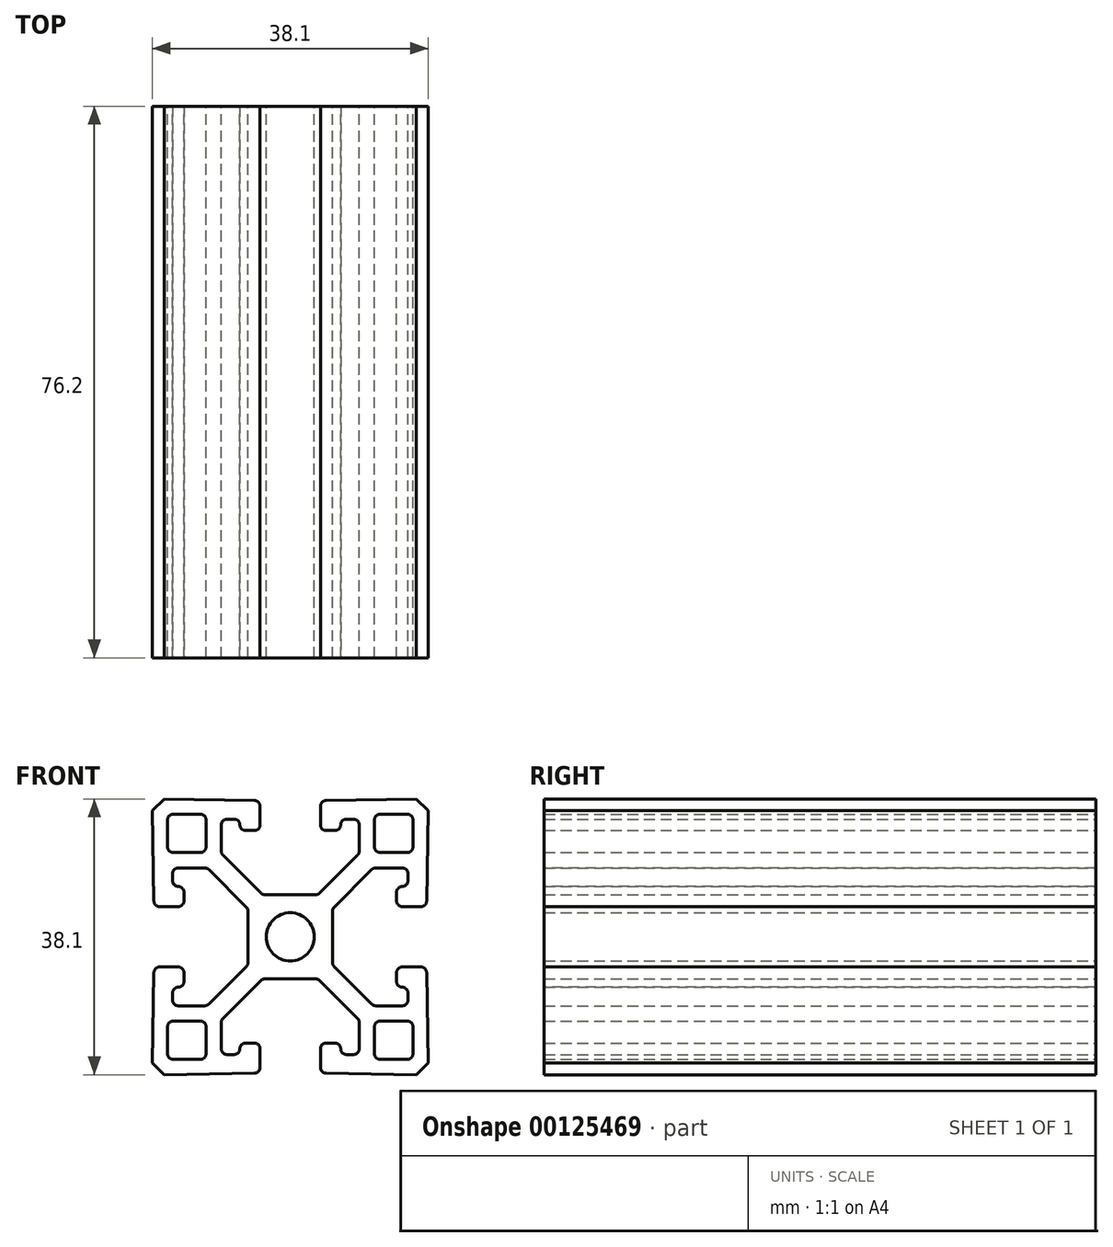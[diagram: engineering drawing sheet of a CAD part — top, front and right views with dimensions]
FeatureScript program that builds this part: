
annotation { "Feature Type Name" : "Feature", "Feature Type Description" : "" }
export const myFeature = defineFeature(function(context is Context, id is Id, definition is map)
    precondition{}
    {
        {
            var Q0;
            Q0=qCreatedBy(makeId("Front.planeOp"),FACE);
            var sketch = newSketch(context, id + "F0", { "sketchPlane" : qUnion([Q0])});
            skCircle(sketch, "E0", {"center": v(-50.07, 14.42) * mm, "radius": 3.33 * mm});
            skLineSegment(sketch, "E1", {"start": v(-33.92, -2.52) * mm, "end": v(-37.65, -2.52) * mm});
            skArc(sketch, "E2", {"start": v(-37.65, -2.52) * mm, "mid": v(-38.2, -2.3) * mm, "end": v(-38.44, -1.74) * mm});
            skLineSegment(sketch, "E3", {"start": v(-38.44, -1.74) * mm, "end": v(-38.44, 2) * mm});
            skArc(sketch, "E4", {"start": v(-38.44, 2) * mm, "mid": v(-38.2, 2.56) * mm, "end": v(-37.65, 2.79) * mm});
            skLineSegment(sketch, "E5", {"start": v(-37.65, 2.79) * mm, "end": v(-33.92, 2.79) * mm});
            skArc(sketch, "E6", {"start": v(-33.92, 2.79) * mm, "mid": v(-33.36, 2.56) * mm, "end": v(-33.13, 2) * mm});
            skLineSegment(sketch, "E7", {"start": v(-33.13, 2) * mm, "end": v(-33.13, -1.74) * mm});
            skArc(sketch, "E8", {"start": v(-33.13, -1.74) * mm, "mid": v(-33.36, -2.3) * mm, "end": v(-33.92, -2.52) * mm});
            skLineSegment(sketch, "E9", {"start": v(-67.01, 2) * mm, "end": v(-67.01, -1.74) * mm});
            skArc(sketch, "E10", {"start": v(-67.01, -1.74) * mm, "mid": v(-66.78, -2.3) * mm, "end": v(-66.23, -2.52) * mm});
            skLineSegment(sketch, "E11", {"start": v(-66.23, -2.52) * mm, "end": v(-62.5, -2.52) * mm});
            skArc(sketch, "E12", {"start": v(-62.5, -2.52) * mm, "mid": v(-61.93, -2.3) * mm, "end": v(-61.7, -1.74) * mm});
            skLineSegment(sketch, "E13", {"start": v(-61.7, -1.74) * mm, "end": v(-61.7, 2) * mm});
            skArc(sketch, "E14", {"start": v(-61.7, 2) * mm, "mid": v(-61.93, 2.56) * mm, "end": v(-62.5, 2.79) * mm});
            skLineSegment(sketch, "E15", {"start": v(-62.5, 2.79) * mm, "end": v(-66.23, 2.79) * mm});
            skArc(sketch, "E16", {"start": v(-66.23, 2.79) * mm, "mid": v(-66.78, 2.56) * mm, "end": v(-67.01, 2) * mm});
            skLineSegment(sketch, "E17", {"start": v(-67.01, 30.57) * mm, "end": v(-67.01, 26.84) * mm});
            skArc(sketch, "E18", {"start": v(-67.01, 26.84) * mm, "mid": v(-66.78, 26.28) * mm, "end": v(-66.23, 26.05) * mm});
            skLineSegment(sketch, "E19", {"start": v(-66.23, 26.05) * mm, "end": v(-62.5, 26.05) * mm});
            skArc(sketch, "E20", {"start": v(-62.5, 26.05) * mm, "mid": v(-61.93, 26.28) * mm, "end": v(-61.7, 26.84) * mm});
            skLineSegment(sketch, "E21", {"start": v(-61.7, 26.84) * mm, "end": v(-61.7, 30.57) * mm});
            skArc(sketch, "E22", {"start": v(-61.7, 30.57) * mm, "mid": v(-61.93, 31.13) * mm, "end": v(-62.5, 31.36) * mm});
            skLineSegment(sketch, "E23", {"start": v(-62.5, 31.36) * mm, "end": v(-66.23, 31.36) * mm});
            skArc(sketch, "E24", {"start": v(-66.23, 31.36) * mm, "mid": v(-66.78, 31.13) * mm, "end": v(-67.01, 30.57) * mm});
            skArc(sketch, "E25", {"start": v(-37.65, 26.05) * mm, "mid": v(-38.2, 26.28) * mm, "end": v(-38.44, 26.84) * mm});
            skLineSegment(sketch, "E26", {"start": v(-38.44, 26.84) * mm, "end": v(-38.44, 30.57) * mm});
            skArc(sketch, "E27", {"start": v(-38.44, 30.57) * mm, "mid": v(-38.2, 31.13) * mm, "end": v(-37.65, 31.36) * mm});
            skLineSegment(sketch, "E28", {"start": v(-37.65, 31.36) * mm, "end": v(-33.92, 31.36) * mm});
            skArc(sketch, "E29", {"start": v(-33.92, 31.36) * mm, "mid": v(-33.36, 31.13) * mm, "end": v(-33.13, 30.57) * mm});
            skLineSegment(sketch, "E30", {"start": v(-33.13, 30.57) * mm, "end": v(-33.13, 26.84) * mm});
            skArc(sketch, "E31", {"start": v(-33.13, 26.84) * mm, "mid": v(-33.36, 26.28) * mm, "end": v(-33.92, 26.05) * mm});
            skLineSegment(sketch, "E32", {"start": v(-33.92, 26.05) * mm, "end": v(-37.65, 26.05) * mm});
            skArc(sketch, "E33", {"start": v(-56.24, -0.26) * mm, "mid": v(-56.8, -0.5) * mm, "end": v(-57.03, -1.05) * mm});
            skLineSegment(sketch, "E34", {"start": v(-56.24, -0.26) * mm, "end": v(-55.02, -0.26) * mm});
            skArc(sketch, "E35", {"start": v(-54.24, -1.05) * mm, "mid": v(-54.47, -0.5) * mm, "end": v(-55.02, -0.26) * mm});
            skLineSegment(sketch, "E36", {"start": v(-54.24, -1.05) * mm, "end": v(-54.24, -3.63) * mm});
            skArc(sketch, "E37", {"start": v(-55.01, -4.41) * mm, "mid": v(-54.46, -4.18) * mm, "end": v(-54.24, -3.63) * mm});
            skLineSegment(sketch, "E38", {"start": v(-55.01, -4.41) * mm, "end": v(-67.5, -4.63) * mm});
            skLineSegment(sketch, "E39", {"start": v(-67.5, -4.63) * mm, "end": v(-69.12, -3) * mm});
            skLineSegment(sketch, "E40", {"start": v(-69.12, -3) * mm, "end": v(-68.9, 9.48) * mm});
            skArc(sketch, "E41", {"start": v(-68.12, 10.25) * mm, "mid": v(-68.67, 10.03) * mm, "end": v(-68.9, 9.48) * mm});
            skLineSegment(sketch, "E42", {"start": v(-68.12, 10.25) * mm, "end": v(-65.54, 10.25) * mm});
            skArc(sketch, "E43", {"start": v(-64.75, 9.47) * mm, "mid": v(-64.98, 10.02) * mm, "end": v(-65.54, 10.25) * mm});
            skLineSegment(sketch, "E44", {"start": v(-64.75, 9.47) * mm, "end": v(-64.75, 8.25) * mm});
            skArc(sketch, "E45", {"start": v(-65.54, 7.46) * mm, "mid": v(-64.98, 7.7) * mm, "end": v(-64.75, 8.25) * mm});
            skArc(sketch, "E46", {"start": v(-65.54, 7.46) * mm, "mid": v(-66.1, 7.23) * mm, "end": v(-66.33, 6.67) * mm});
            skLineSegment(sketch, "E47", {"start": v(-66.33, 6.67) * mm, "end": v(-66.33, 5.68) * mm});
            skArc(sketch, "E48", {"start": v(-66.33, 5.68) * mm, "mid": v(-66.1, 5.12) * mm, "end": v(-65.54, 4.9) * mm});
            skLineSegment(sketch, "E49", {"start": v(-65.54, 4.9) * mm, "end": v(-61.9, 4.9) * mm});
            skArc(sketch, "E50", {"start": v(-61.9, 4.9) * mm, "mid": v(-61.6, 4.95) * mm, "end": v(-61.34, 5.12) * mm});
            skLineSegment(sketch, "E51", {"start": v(-61.34, 5.12) * mm, "end": v(-56.12, 10.35) * mm});
            skArc(sketch, "E52", {"start": v(-56.12, 10.35) * mm, "mid": v(-55.95, 10.6) * mm, "end": v(-55.89, 10.9) * mm});
            skLineSegment(sketch, "E53", {"start": v(-55.89, 10.9) * mm, "end": v(-55.89, 17.93) * mm});
            skArc(sketch, "E54", {"start": v(-55.89, 17.93) * mm, "mid": v(-55.95, 18.24) * mm, "end": v(-56.12, 18.5) * mm});
            skLineSegment(sketch, "E55", {"start": v(-56.12, 18.5) * mm, "end": v(-61.34, 23.71) * mm});
            skArc(sketch, "E56", {"start": v(-61.34, 23.71) * mm, "mid": v(-61.6, 23.88) * mm, "end": v(-61.9, 23.94) * mm});
            skLineSegment(sketch, "E57", {"start": v(-61.9, 23.94) * mm, "end": v(-65.54, 23.94) * mm});
            skArc(sketch, "E58", {"start": v(-65.54, 23.94) * mm, "mid": v(-66.1, 23.71) * mm, "end": v(-66.33, 23.16) * mm});
            skLineSegment(sketch, "E59", {"start": v(-66.33, 23.16) * mm, "end": v(-66.33, 22.17) * mm});
            skArc(sketch, "E60", {"start": v(-66.33, 22.17) * mm, "mid": v(-66.1, 21.6) * mm, "end": v(-65.54, 21.38) * mm});
            skArc(sketch, "E61", {"start": v(-64.75, 20.6) * mm, "mid": v(-64.98, 21.15) * mm, "end": v(-65.54, 21.38) * mm});
            skLineSegment(sketch, "E62", {"start": v(-64.75, 20.6) * mm, "end": v(-64.75, 19.37) * mm});
            skArc(sketch, "E63", {"start": v(-65.54, 18.58) * mm, "mid": v(-64.98, 18.82) * mm, "end": v(-64.75, 19.37) * mm});
            skLineSegment(sketch, "E64", {"start": v(-65.54, 18.58) * mm, "end": v(-68.12, 18.58) * mm});
            skArc(sketch, "E65", {"start": v(-68.9, 19.36) * mm, "mid": v(-68.67, 18.81) * mm, "end": v(-68.12, 18.58) * mm});
            skLineSegment(sketch, "E66", {"start": v(-68.9, 19.36) * mm, "end": v(-69.12, 31.84) * mm});
            skLineSegment(sketch, "E67", {"start": v(-69.12, 31.84) * mm, "end": v(-67.5, 33.47) * mm});
            skLineSegment(sketch, "E68", {"start": v(-67.5, 33.47) * mm, "end": v(-55.01, 33.25) * mm});
            skArc(sketch, "E69", {"start": v(-54.24, 32.46) * mm, "mid": v(-54.46, 33.02) * mm, "end": v(-55.01, 33.25) * mm});
            skLineSegment(sketch, "E70", {"start": v(-54.24, 32.46) * mm, "end": v(-54.24, 29.89) * mm});
            skArc(sketch, "E71", {"start": v(-55.02, 29.1) * mm, "mid": v(-54.47, 29.33) * mm, "end": v(-54.24, 29.89) * mm});
            skLineSegment(sketch, "E72", {"start": v(-55.02, 29.1) * mm, "end": v(-56.24, 29.1) * mm});
            skArc(sketch, "E73", {"start": v(-57.03, 29.89) * mm, "mid": v(-56.8, 29.33) * mm, "end": v(-56.24, 29.1) * mm});
            skArc(sketch, "E74", {"start": v(-57.03, 29.89) * mm, "mid": v(-57.26, 30.44) * mm, "end": v(-57.82, 30.68) * mm});
            skLineSegment(sketch, "E75", {"start": v(-57.82, 30.68) * mm, "end": v(-58.8, 30.68) * mm});
            skArc(sketch, "E76", {"start": v(-58.8, 30.68) * mm, "mid": v(-59.37, 30.44) * mm, "end": v(-59.6, 29.89) * mm});
            skLineSegment(sketch, "E77", {"start": v(-59.6, 29.89) * mm, "end": v(-59.6, 26.25) * mm});
            skArc(sketch, "E78", {"start": v(-59.6, 26.25) * mm, "mid": v(-59.54, 25.94) * mm, "end": v(-59.37, 25.69) * mm});
            skLineSegment(sketch, "E79", {"start": v(-59.37, 25.69) * mm, "end": v(-54.14, 20.47) * mm});
            skArc(sketch, "E80", {"start": v(-54.14, 20.47) * mm, "mid": v(-53.89, 20.3) * mm, "end": v(-53.59, 20.24) * mm});
            skLineSegment(sketch, "E81", {"start": v(-53.59, 20.24) * mm, "end": v(-46.56, 20.24) * mm});
            skArc(sketch, "E82", {"start": v(-46.56, 20.24) * mm, "mid": v(-46.25, 20.3) * mm, "end": v(-46, 20.47) * mm});
            skLineSegment(sketch, "E83", {"start": v(-46, 20.47) * mm, "end": v(-40.78, 25.69) * mm});
            skArc(sketch, "E84", {"start": v(-40.78, 25.69) * mm, "mid": v(-40.6, 25.94) * mm, "end": v(-40.55, 26.25) * mm});
            skLineSegment(sketch, "E85", {"start": v(-40.55, 26.25) * mm, "end": v(-40.55, 29.89) * mm});
            skArc(sketch, "E86", {"start": v(-40.55, 29.89) * mm, "mid": v(-40.78, 30.44) * mm, "end": v(-41.33, 30.68) * mm});
            skLineSegment(sketch, "E87", {"start": v(-41.33, 30.68) * mm, "end": v(-42.32, 30.68) * mm});
            skArc(sketch, "E88", {"start": v(-42.32, 30.68) * mm, "mid": v(-42.88, 30.44) * mm, "end": v(-43.11, 29.89) * mm});
            skArc(sketch, "E89", {"start": v(-43.9, 29.1) * mm, "mid": v(-43.34, 29.33) * mm, "end": v(-43.11, 29.89) * mm});
            skLineSegment(sketch, "E90", {"start": v(-43.9, 29.1) * mm, "end": v(-45.12, 29.1) * mm});
            skArc(sketch, "E91", {"start": v(-45.9, 29.89) * mm, "mid": v(-45.67, 29.33) * mm, "end": v(-45.12, 29.1) * mm});
            skLineSegment(sketch, "E92", {"start": v(-45.9, 29.89) * mm, "end": v(-45.9, 32.46) * mm});
            skArc(sketch, "E93", {"start": v(-45.13, 33.25) * mm, "mid": v(-45.68, 33.02) * mm, "end": v(-45.9, 32.46) * mm});
            skLineSegment(sketch, "E94", {"start": v(-45.13, 33.25) * mm, "end": v(-32.65, 33.47) * mm});
            skLineSegment(sketch, "E95", {"start": v(-32.65, 33.47) * mm, "end": v(-31.02, 31.84) * mm});
            skLineSegment(sketch, "E96", {"start": v(-31.02, 31.84) * mm, "end": v(-31.24, 19.36) * mm});
            skArc(sketch, "E97", {"start": v(-32.03, 18.58) * mm, "mid": v(-31.47, 18.81) * mm, "end": v(-31.24, 19.36) * mm});
            skLineSegment(sketch, "E98", {"start": v(-32.03, 18.58) * mm, "end": v(-34.6, 18.58) * mm});
            skArc(sketch, "E99", {"start": v(-35.39, 19.37) * mm, "mid": v(-35.16, 18.82) * mm, "end": v(-34.6, 18.58) * mm});
            skLineSegment(sketch, "E100", {"start": v(-35.39, 19.37) * mm, "end": v(-35.39, 20.6) * mm});
            skArc(sketch, "E101", {"start": v(-34.6, 21.38) * mm, "mid": v(-35.16, 21.15) * mm, "end": v(-35.39, 20.6) * mm});
            skArc(sketch, "E102", {"start": v(-34.6, 21.38) * mm, "mid": v(-34.05, 21.6) * mm, "end": v(-33.81, 22.17) * mm});
            skLineSegment(sketch, "E103", {"start": v(-33.81, 22.17) * mm, "end": v(-33.81, 23.16) * mm});
            skArc(sketch, "E104", {"start": v(-33.81, 23.16) * mm, "mid": v(-34.05, 23.71) * mm, "end": v(-34.6, 23.94) * mm});
            skLineSegment(sketch, "E105", {"start": v(-34.6, 23.94) * mm, "end": v(-38.24, 23.94) * mm});
            skArc(sketch, "E106", {"start": v(-38.24, 23.94) * mm, "mid": v(-38.55, 23.88) * mm, "end": v(-38.8, 23.71) * mm});
            skLineSegment(sketch, "E107", {"start": v(-38.8, 23.71) * mm, "end": v(-44.02, 18.5) * mm});
            skArc(sketch, "E108", {"start": v(-44.02, 18.5) * mm, "mid": v(-44.2, 18.24) * mm, "end": v(-44.25, 17.93) * mm});
            skLineSegment(sketch, "E109", {"start": v(-44.25, 17.93) * mm, "end": v(-44.25, 10.9) * mm});
            skArc(sketch, "E110", {"start": v(-44.25, 10.9) * mm, "mid": v(-44.2, 10.6) * mm, "end": v(-44.02, 10.35) * mm});
            skLineSegment(sketch, "E111", {"start": v(-44.02, 10.35) * mm, "end": v(-38.8, 5.12) * mm});
            skArc(sketch, "E112", {"start": v(-38.8, 5.12) * mm, "mid": v(-38.55, 4.95) * mm, "end": v(-38.24, 4.9) * mm});
            skLineSegment(sketch, "E113", {"start": v(-38.24, 4.9) * mm, "end": v(-34.6, 4.9) * mm});
            skArc(sketch, "E114", {"start": v(-34.6, 4.9) * mm, "mid": v(-34.05, 5.12) * mm, "end": v(-33.81, 5.68) * mm});
            skLineSegment(sketch, "E115", {"start": v(-33.81, 5.68) * mm, "end": v(-33.81, 6.67) * mm});
            skArc(sketch, "E116", {"start": v(-33.81, 6.67) * mm, "mid": v(-34.05, 7.23) * mm, "end": v(-34.6, 7.46) * mm});
            skArc(sketch, "E117", {"start": v(-35.39, 8.25) * mm, "mid": v(-35.16, 7.7) * mm, "end": v(-34.6, 7.46) * mm});
            skLineSegment(sketch, "E118", {"start": v(-35.39, 8.25) * mm, "end": v(-35.39, 9.47) * mm});
            skArc(sketch, "E119", {"start": v(-34.6, 10.25) * mm, "mid": v(-35.16, 10.02) * mm, "end": v(-35.39, 9.47) * mm});
            skLineSegment(sketch, "E120", {"start": v(-34.6, 10.25) * mm, "end": v(-32.03, 10.25) * mm});
            skArc(sketch, "E121", {"start": v(-31.24, 9.48) * mm, "mid": v(-31.47, 10.03) * mm, "end": v(-32.03, 10.25) * mm});
            skLineSegment(sketch, "E122", {"start": v(-31.24, 9.48) * mm, "end": v(-31.02, -3) * mm});
            skLineSegment(sketch, "E123", {"start": v(-31.02, -3) * mm, "end": v(-32.65, -4.63) * mm});
            skLineSegment(sketch, "E124", {"start": v(-32.65, -4.63) * mm, "end": v(-45.13, -4.41) * mm});
            skArc(sketch, "E125", {"start": v(-45.9, -3.63) * mm, "mid": v(-45.68, -4.18) * mm, "end": v(-45.13, -4.41) * mm});
            skLineSegment(sketch, "E126", {"start": v(-45.9, -3.63) * mm, "end": v(-45.9, -1.05) * mm});
            skArc(sketch, "E127", {"start": v(-45.12, -0.26) * mm, "mid": v(-45.67, -0.5) * mm, "end": v(-45.9, -1.05) * mm});
            skLineSegment(sketch, "E128", {"start": v(-45.12, -0.26) * mm, "end": v(-43.9, -0.26) * mm});
            skArc(sketch, "E129", {"start": v(-43.11, -1.05) * mm, "mid": v(-43.34, -0.5) * mm, "end": v(-43.9, -0.26) * mm});
            skArc(sketch, "E130", {"start": v(-43.11, -1.05) * mm, "mid": v(-42.88, -1.6) * mm, "end": v(-42.32, -1.84) * mm});
            skLineSegment(sketch, "E131", {"start": v(-42.32, -1.84) * mm, "end": v(-41.33, -1.84) * mm});
            skArc(sketch, "E132", {"start": v(-41.33, -1.84) * mm, "mid": v(-40.78, -1.6) * mm, "end": v(-40.55, -1.05) * mm});
            skLineSegment(sketch, "E133", {"start": v(-40.55, -1.05) * mm, "end": v(-40.55, 2.6) * mm});
            skArc(sketch, "E134", {"start": v(-40.55, 2.6) * mm, "mid": v(-40.6, 2.9) * mm, "end": v(-40.78, 3.15) * mm});
            skLineSegment(sketch, "E135", {"start": v(-40.78, 3.15) * mm, "end": v(-46, 8.37) * mm});
            skArc(sketch, "E136", {"start": v(-46, 8.37) * mm, "mid": v(-46.25, 8.54) * mm, "end": v(-46.56, 8.6) * mm});
            skLineSegment(sketch, "E137", {"start": v(-46.56, 8.6) * mm, "end": v(-53.59, 8.6) * mm});
            skArc(sketch, "E138", {"start": v(-53.59, 8.6) * mm, "mid": v(-53.89, 8.54) * mm, "end": v(-54.14, 8.37) * mm});
            skLineSegment(sketch, "E139", {"start": v(-54.14, 8.37) * mm, "end": v(-59.37, 3.15) * mm});
            skArc(sketch, "E140", {"start": v(-59.37, 3.15) * mm, "mid": v(-59.54, 2.9) * mm, "end": v(-59.6, 2.6) * mm});
            skLineSegment(sketch, "E141", {"start": v(-59.6, 2.6) * mm, "end": v(-59.6, -1.05) * mm});
            skArc(sketch, "E142", {"start": v(-59.6, -1.05) * mm, "mid": v(-59.37, -1.6) * mm, "end": v(-58.8, -1.84) * mm});
            skLineSegment(sketch, "E143", {"start": v(-58.8, -1.84) * mm, "end": v(-57.82, -1.84) * mm});
            skArc(sketch, "E144", {"start": v(-57.82, -1.84) * mm, "mid": v(-57.26, -1.6) * mm, "end": v(-57.03, -1.05) * mm});
            skLineSegment(sketch, "E145", {"start": v(-61.7, 2) * mm, "end": v(-61.7, -1.74) * mm});
            skArc(sketch, "E146", {"start": v(-61.7, -1.74) * mm, "mid": v(-61.93, -2.3) * mm, "end": v(-62.5, -2.52) * mm});
            skLineSegment(sketch, "E147", {"start": v(-62.5, -2.52) * mm, "end": v(-66.23, -2.52) * mm});
            skArc(sketch, "E148", {"start": v(-66.23, -2.52) * mm, "mid": v(-66.78, -2.3) * mm, "end": v(-67.01, -1.74) * mm});
            skLineSegment(sketch, "E149", {"start": v(-67.01, -1.74) * mm, "end": v(-67.01, 2) * mm});
            skArc(sketch, "E150", {"start": v(-67.01, 2) * mm, "mid": v(-66.78, 2.56) * mm, "end": v(-66.23, 2.79) * mm});
            skLineSegment(sketch, "E151", {"start": v(-66.23, 2.79) * mm, "end": v(-62.5, 2.79) * mm});
            skArc(sketch, "E152", {"start": v(-62.5, 2.79) * mm, "mid": v(-61.93, 2.56) * mm, "end": v(-61.7, 2) * mm});
            skLineSegment(sketch, "E153", {"start": v(-62.5, 26.05) * mm, "end": v(-66.23, 26.05) * mm});
            skArc(sketch, "E154", {"start": v(-66.23, 26.05) * mm, "mid": v(-66.78, 26.28) * mm, "end": v(-67.01, 26.84) * mm});
            skLineSegment(sketch, "E155", {"start": v(-67.01, 26.84) * mm, "end": v(-67.01, 30.57) * mm});
            skArc(sketch, "E156", {"start": v(-67.01, 30.57) * mm, "mid": v(-66.78, 31.13) * mm, "end": v(-66.23, 31.36) * mm});
            skLineSegment(sketch, "E157", {"start": v(-66.23, 31.36) * mm, "end": v(-62.5, 31.36) * mm});
            skArc(sketch, "E158", {"start": v(-62.5, 31.36) * mm, "mid": v(-61.93, 31.13) * mm, "end": v(-61.7, 30.57) * mm});
            skLineSegment(sketch, "E159", {"start": v(-61.7, 30.57) * mm, "end": v(-61.7, 26.84) * mm});
            skArc(sketch, "E160", {"start": v(-61.7, 26.84) * mm, "mid": v(-61.93, 26.28) * mm, "end": v(-62.5, 26.05) * mm});
            skArc(sketch, "E161", {"start": v(-46.74, 14.42) * mm, "mid": v(-50.07, 11.1) * mm, "end": v(-53.4, 14.42) * mm});
            skArc(sketch, "E162", {"start": v(-53.4, 14.42) * mm, "mid": v(-50.07, 17.75) * mm, "end": v(-46.74, 14.42) * mm});
            skArc(sketch, "E163", {"start": v(-38.8, 23.71) * mm, "mid": v(-38.55, 23.88) * mm, "end": v(-38.24, 23.94) * mm});
            skLineSegment(sketch, "E164", {"start": v(-38.24, 23.94) * mm, "end": v(-34.6, 23.94) * mm});
            skArc(sketch, "E165", {"start": v(-34.6, 23.94) * mm, "mid": v(-34.05, 23.71) * mm, "end": v(-33.81, 23.16) * mm});
            skLineSegment(sketch, "E166", {"start": v(-33.81, 23.16) * mm, "end": v(-33.81, 22.17) * mm});
            skArc(sketch, "E167", {"start": v(-33.81, 22.17) * mm, "mid": v(-34.05, 21.6) * mm, "end": v(-34.6, 21.38) * mm});
            skLineSegment(sketch, "E168", {"start": v(-35.39, 20.6) * mm, "end": v(-35.39, 19.37) * mm});
            skLineSegment(sketch, "E169", {"start": v(-34.6, 18.58) * mm, "end": v(-32.03, 18.58) * mm});
            skLineSegment(sketch, "E170", {"start": v(-31.24, 19.36) * mm, "end": v(-31.02, 31.84) * mm});
            skLineSegment(sketch, "E171", {"start": v(-31.02, 31.84) * mm, "end": v(-32.65, 33.47) * mm});
            skLineSegment(sketch, "E172", {"start": v(-32.65, 33.47) * mm, "end": v(-45.13, 33.25) * mm});
            skLineSegment(sketch, "E173", {"start": v(-45.9, 32.46) * mm, "end": v(-45.9, 29.89) * mm});
            skLineSegment(sketch, "E174", {"start": v(-45.12, 29.1) * mm, "end": v(-43.9, 29.1) * mm});
            skArc(sketch, "E175", {"start": v(-43.11, 29.89) * mm, "mid": v(-42.88, 30.44) * mm, "end": v(-42.32, 30.68) * mm});
            skLineSegment(sketch, "E176", {"start": v(-42.32, 30.68) * mm, "end": v(-41.33, 30.68) * mm});
            skArc(sketch, "E177", {"start": v(-41.33, 30.68) * mm, "mid": v(-40.78, 30.44) * mm, "end": v(-40.55, 29.89) * mm});
            skLineSegment(sketch, "E178", {"start": v(-40.55, 29.89) * mm, "end": v(-40.55, 26.25) * mm});
            skArc(sketch, "E179", {"start": v(-40.55, 26.25) * mm, "mid": v(-40.6, 25.94) * mm, "end": v(-40.78, 25.69) * mm});
            skLineSegment(sketch, "E180", {"start": v(-40.78, 25.69) * mm, "end": v(-46, 20.47) * mm});
            skArc(sketch, "E181", {"start": v(-46, 20.47) * mm, "mid": v(-46.25, 20.3) * mm, "end": v(-46.56, 20.24) * mm});
            skLineSegment(sketch, "E182", {"start": v(-46.56, 20.24) * mm, "end": v(-53.59, 20.24) * mm});
            skArc(sketch, "E183", {"start": v(-53.59, 20.24) * mm, "mid": v(-53.89, 20.3) * mm, "end": v(-54.14, 20.47) * mm});
            skLineSegment(sketch, "E184", {"start": v(-54.14, 20.47) * mm, "end": v(-59.37, 25.69) * mm});
            skArc(sketch, "E185", {"start": v(-59.37, 25.69) * mm, "mid": v(-59.54, 25.94) * mm, "end": v(-59.6, 26.25) * mm});
            skLineSegment(sketch, "E186", {"start": v(-59.6, 26.25) * mm, "end": v(-59.6, 29.89) * mm});
            skArc(sketch, "E187", {"start": v(-59.6, 29.89) * mm, "mid": v(-59.37, 30.44) * mm, "end": v(-58.8, 30.68) * mm});
            skLineSegment(sketch, "E188", {"start": v(-58.8, 30.68) * mm, "end": v(-57.82, 30.68) * mm});
            skArc(sketch, "E189", {"start": v(-57.82, 30.68) * mm, "mid": v(-57.26, 30.44) * mm, "end": v(-57.03, 29.89) * mm});
            skLineSegment(sketch, "E190", {"start": v(-56.24, 29.1) * mm, "end": v(-55.02, 29.1) * mm});
            skLineSegment(sketch, "E191", {"start": v(-54.24, 29.89) * mm, "end": v(-54.24, 32.46) * mm});
            skLineSegment(sketch, "E192", {"start": v(-55.01, 33.25) * mm, "end": v(-67.5, 33.47) * mm});
            skLineSegment(sketch, "E193", {"start": v(-67.5, 33.47) * mm, "end": v(-69.12, 31.84) * mm});
            skLineSegment(sketch, "E194", {"start": v(-69.12, 31.84) * mm, "end": v(-68.9, 19.36) * mm});
            skLineSegment(sketch, "E195", {"start": v(-68.12, 18.58) * mm, "end": v(-65.54, 18.58) * mm});
            skLineSegment(sketch, "E196", {"start": v(-64.75, 19.37) * mm, "end": v(-64.75, 20.6) * mm});
            skArc(sketch, "E197", {"start": v(-65.54, 21.38) * mm, "mid": v(-66.1, 21.6) * mm, "end": v(-66.33, 22.17) * mm});
            skLineSegment(sketch, "E198", {"start": v(-66.33, 22.17) * mm, "end": v(-66.33, 23.16) * mm});
            skArc(sketch, "E199", {"start": v(-66.33, 23.16) * mm, "mid": v(-66.1, 23.71) * mm, "end": v(-65.54, 23.94) * mm});
            skLineSegment(sketch, "E200", {"start": v(-65.54, 23.94) * mm, "end": v(-61.9, 23.94) * mm});
            skArc(sketch, "E201", {"start": v(-61.9, 23.94) * mm, "mid": v(-61.6, 23.88) * mm, "end": v(-61.34, 23.71) * mm});
            skLineSegment(sketch, "E202", {"start": v(-61.34, 23.71) * mm, "end": v(-56.12, 18.5) * mm});
            skArc(sketch, "E203", {"start": v(-56.12, 18.5) * mm, "mid": v(-55.95, 18.24) * mm, "end": v(-55.89, 17.93) * mm});
            skLineSegment(sketch, "E204", {"start": v(-55.89, 17.93) * mm, "end": v(-55.89, 10.9) * mm});
            skArc(sketch, "E205", {"start": v(-55.89, 10.9) * mm, "mid": v(-55.95, 10.6) * mm, "end": v(-56.12, 10.35) * mm});
            skLineSegment(sketch, "E206", {"start": v(-56.12, 10.35) * mm, "end": v(-61.34, 5.12) * mm});
            skArc(sketch, "E207", {"start": v(-61.34, 5.12) * mm, "mid": v(-61.6, 4.95) * mm, "end": v(-61.9, 4.9) * mm});
            skLineSegment(sketch, "E208", {"start": v(-61.9, 4.9) * mm, "end": v(-65.54, 4.9) * mm});
            skArc(sketch, "E209", {"start": v(-65.54, 4.9) * mm, "mid": v(-66.1, 5.12) * mm, "end": v(-66.33, 5.68) * mm});
            skLineSegment(sketch, "E210", {"start": v(-66.33, 5.68) * mm, "end": v(-66.33, 6.67) * mm});
            skArc(sketch, "E211", {"start": v(-66.33, 6.67) * mm, "mid": v(-66.1, 7.23) * mm, "end": v(-65.54, 7.46) * mm});
            skLineSegment(sketch, "E212", {"start": v(-64.75, 8.25) * mm, "end": v(-64.75, 9.47) * mm});
            skLineSegment(sketch, "E213", {"start": v(-65.54, 10.25) * mm, "end": v(-68.12, 10.25) * mm});
            skLineSegment(sketch, "E214", {"start": v(-68.9, 9.48) * mm, "end": v(-69.12, -3) * mm});
            skLineSegment(sketch, "E215", {"start": v(-69.12, -3) * mm, "end": v(-67.5, -4.63) * mm});
            skLineSegment(sketch, "E216", {"start": v(-67.5, -4.63) * mm, "end": v(-55.01, -4.41) * mm});
            skLineSegment(sketch, "E217", {"start": v(-54.24, -3.63) * mm, "end": v(-54.24, -1.05) * mm});
            skLineSegment(sketch, "E218", {"start": v(-55.02, -0.26) * mm, "end": v(-56.24, -0.26) * mm});
            skArc(sketch, "E219", {"start": v(-57.03, -1.05) * mm, "mid": v(-57.26, -1.6) * mm, "end": v(-57.82, -1.84) * mm});
            skLineSegment(sketch, "E220", {"start": v(-57.82, -1.84) * mm, "end": v(-58.8, -1.84) * mm});
            skArc(sketch, "E221", {"start": v(-58.8, -1.84) * mm, "mid": v(-59.37, -1.6) * mm, "end": v(-59.6, -1.05) * mm});
            skLineSegment(sketch, "E222", {"start": v(-59.6, -1.05) * mm, "end": v(-59.6, 2.6) * mm});
            skArc(sketch, "E223", {"start": v(-59.6, 2.6) * mm, "mid": v(-59.54, 2.9) * mm, "end": v(-59.37, 3.15) * mm});
            skLineSegment(sketch, "E224", {"start": v(-59.37, 3.15) * mm, "end": v(-54.14, 8.37) * mm});
            skArc(sketch, "E225", {"start": v(-54.14, 8.37) * mm, "mid": v(-53.89, 8.54) * mm, "end": v(-53.59, 8.6) * mm});
            skLineSegment(sketch, "E226", {"start": v(-53.59, 8.6) * mm, "end": v(-46.56, 8.6) * mm});
            skArc(sketch, "E227", {"start": v(-46.56, 8.6) * mm, "mid": v(-46.25, 8.54) * mm, "end": v(-46, 8.37) * mm});
            skLineSegment(sketch, "E228", {"start": v(-46, 8.37) * mm, "end": v(-40.78, 3.15) * mm});
            skArc(sketch, "E229", {"start": v(-40.78, 3.15) * mm, "mid": v(-40.6, 2.9) * mm, "end": v(-40.55, 2.6) * mm});
            skLineSegment(sketch, "E230", {"start": v(-40.55, 2.6) * mm, "end": v(-40.55, -1.05) * mm});
            skArc(sketch, "E231", {"start": v(-40.55, -1.05) * mm, "mid": v(-40.78, -1.6) * mm, "end": v(-41.33, -1.84) * mm});
            skLineSegment(sketch, "E232", {"start": v(-41.33, -1.84) * mm, "end": v(-42.32, -1.84) * mm});
            skArc(sketch, "E233", {"start": v(-42.32, -1.84) * mm, "mid": v(-42.88, -1.6) * mm, "end": v(-43.11, -1.05) * mm});
            skLineSegment(sketch, "E234", {"start": v(-43.9, -0.26) * mm, "end": v(-45.12, -0.26) * mm});
            skLineSegment(sketch, "E235", {"start": v(-45.9, -1.05) * mm, "end": v(-45.9, -3.63) * mm});
            skLineSegment(sketch, "E236", {"start": v(-45.13, -4.41) * mm, "end": v(-32.65, -4.63) * mm});
            skLineSegment(sketch, "E237", {"start": v(-32.65, -4.63) * mm, "end": v(-31.02, -3) * mm});
            skLineSegment(sketch, "E238", {"start": v(-31.02, -3) * mm, "end": v(-31.24, 9.48) * mm});
            skLineSegment(sketch, "E239", {"start": v(-32.03, 10.25) * mm, "end": v(-34.6, 10.25) * mm});
            skLineSegment(sketch, "E240", {"start": v(-35.39, 9.47) * mm, "end": v(-35.39, 8.25) * mm});
            skArc(sketch, "E241", {"start": v(-34.6, 7.46) * mm, "mid": v(-34.05, 7.23) * mm, "end": v(-33.81, 6.67) * mm});
            skLineSegment(sketch, "E242", {"start": v(-33.81, 6.67) * mm, "end": v(-33.81, 5.68) * mm});
            skArc(sketch, "E243", {"start": v(-33.81, 5.68) * mm, "mid": v(-34.05, 5.12) * mm, "end": v(-34.6, 4.9) * mm});
            skLineSegment(sketch, "E244", {"start": v(-34.6, 4.9) * mm, "end": v(-38.24, 4.9) * mm});
            skArc(sketch, "E245", {"start": v(-38.24, 4.9) * mm, "mid": v(-38.55, 4.95) * mm, "end": v(-38.8, 5.12) * mm});
            skLineSegment(sketch, "E246", {"start": v(-38.8, 5.12) * mm, "end": v(-44.02, 10.35) * mm});
            skArc(sketch, "E247", {"start": v(-44.02, 10.35) * mm, "mid": v(-44.2, 10.6) * mm, "end": v(-44.25, 10.9) * mm});
            skLineSegment(sketch, "E248", {"start": v(-44.25, 10.9) * mm, "end": v(-44.25, 17.93) * mm});
            skArc(sketch, "E249", {"start": v(-44.25, 17.93) * mm, "mid": v(-44.2, 18.24) * mm, "end": v(-44.02, 18.5) * mm});
            skLineSegment(sketch, "E250", {"start": v(-44.02, 18.5) * mm, "end": v(-38.8, 23.71) * mm});
            skSolve(sketch);
        }
        {
            var Q0;
            Q0 = qSketchRegion(id + "F0", true);
            extrude(context, id + "F1", {"entities" : qUnion([Q0]), "depth" : 76.2 * mm});
        }
    });
